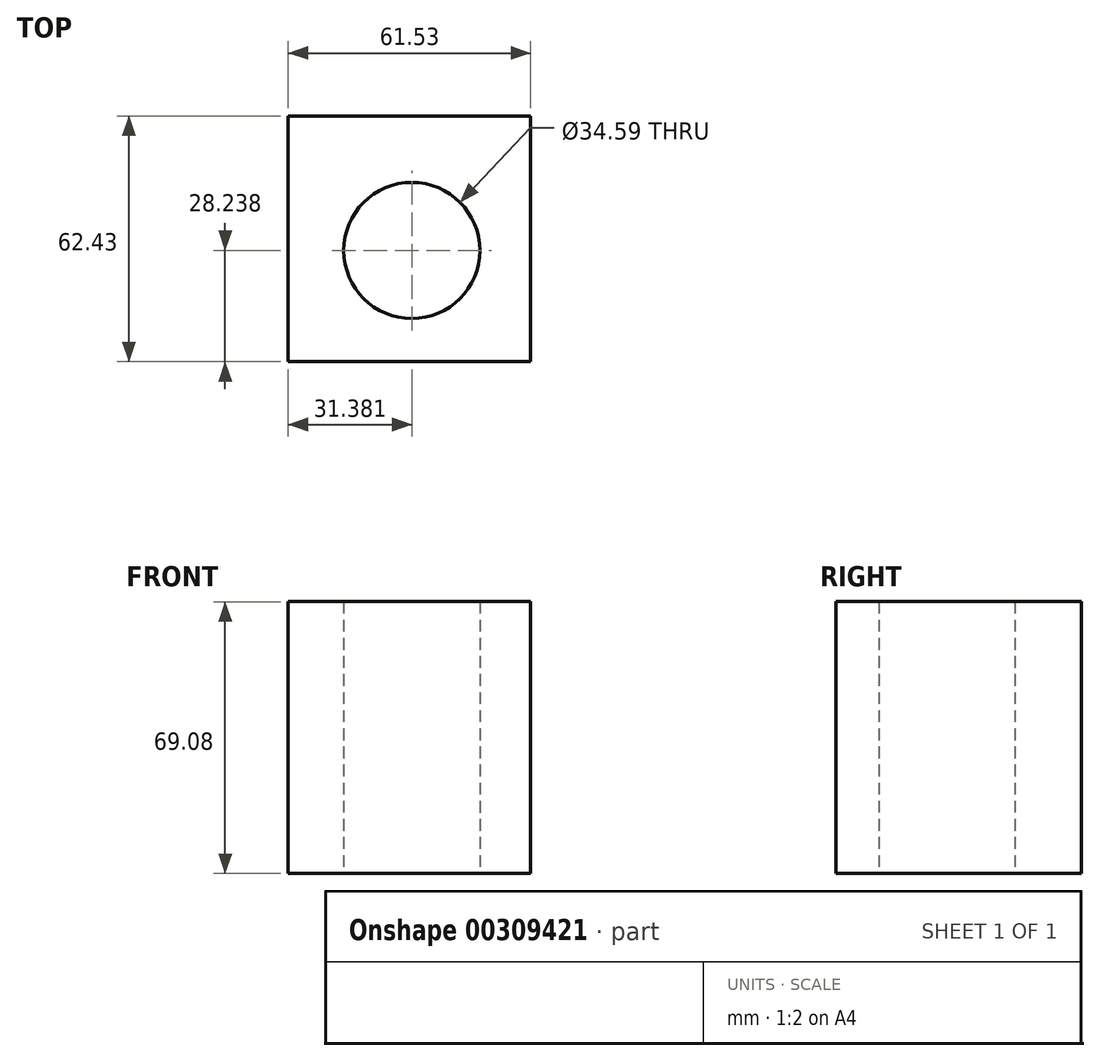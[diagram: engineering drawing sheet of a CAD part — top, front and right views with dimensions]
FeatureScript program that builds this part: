
annotation { "Feature Type Name" : "Feature", "Feature Type Description" : "" }
export const myFeature = defineFeature(function(context is Context, id is Id, definition is map)
    precondition{}
    {
        {
            var Q0;
            Q0=qCreatedBy(makeId("Top.planeOp"),FACE);
            var sketch = newSketch(context, id + "F0", { "sketchPlane" : qUnion([Q0])});
            skLineSegment(sketch, "E0.bottom", {"start": v(0, 0) * mm, "end": v(-61.53, 0) * mm});
            skLineSegment(sketch, "E0.top", {"start": v(0, 62.43) * mm, "end": v(-61.53, 62.43) * mm});
            skLineSegment(sketch, "E0.left", {"start": v(0, 0) * mm, "end": v(0, 62.43) * mm});
            skLineSegment(sketch, "E0.right", {"start": v(-61.53, 0) * mm, "end": v(-61.53, 62.43) * mm});
            skCircle(sketch, "E1", {"center": v(-30.15, 28.24) * mm, "radius": 17.3 * mm});
            skSolve(sketch);
        }
        {
            var Q0;
            Q0 = qSketchRegion(id + "F0", true);
            extrude(context, id + "F1", {"entities" : qUnion([Q0]), "endBound" : BoundingType.SYMMETRIC, "depth" : 69.1 * mm});
        }
    });
